# Revit family: EDFP210C
name_source: partatom
category: Plumbing Fixtures
units: mm (PartAtom-declared; Revit-internal decimal feet)

## family parameters
Always vertical = Yes
Cut with Voids When Loaded = No
OmniClass Number = 23.45.00.00
OmniClass Title = Sanitary, Laundry, and Cleaning Equipment
Part Type = Normal
Room Calculation Point = No
Round Connector Dimension = Use Diameter
Shared = No
Work Plane-Based = No

## types (3) — shared parameters
Activation by = Mechanical Front Bubbler Button
Approx. Shipping Weight = 14 lbs.
Assembly Code = D2010810
BUBBLER_MATERIAL = Metal - Steel - Stainless - Chrome
BUTTON_MATERIAL = Metal - Steel - Stainless - Chrome
Bubbler Style = Flexi-Guard ® Safety Bubbler
CW Connection = Yes
Chilling Option = Non-refrigerated
DRAIN_MATERIAL = Metal - Steel - Stainless - Chrome
Description = Elkay Soft Sides Single Composite Fountain Non-Filtered, Non-Refrigerated White Granite Composite
Dimensions (L x W x H) = 12 1/8inch x 13inch x 6 1/2Inch
Drain_Pipe 1 1/2" = 38 mm
Finish = Stainless Steel
HW Connection = No
Inlet_Pipe = 10 mm  [stored 0.0328084 ft]
Installation Location = Indoor + Outdoor
Manufacturer = Elkay
Model = EDFP210C
Mounting Type = Wall Mount (On Wall)
No. of Stations Served = 1
Power = No Electrical Required
SINK_MATERIAL = Metal - Steel - Stainless - Chrome
Vent Connection = No
Version = 1.0.0.0
Waste Connection = Yes

## per-type parameters (varying)
| type | BODY_MATERIAL |
| EDFP210C | Metal - Steel - Stainless - Chrome |
| EDFP210FPK | Metal - Steel - Stainless - Chrome |
| EDFP210RC | WHT-White Granite Composite |

note: [stored X ft] marks values corroborated as IEEE doubles in the binary element streams (Revit-internal decimal feet)

## geometry (parser evidence)
native form markers: Sweep x18
no freeform markers — native parametric forms only
